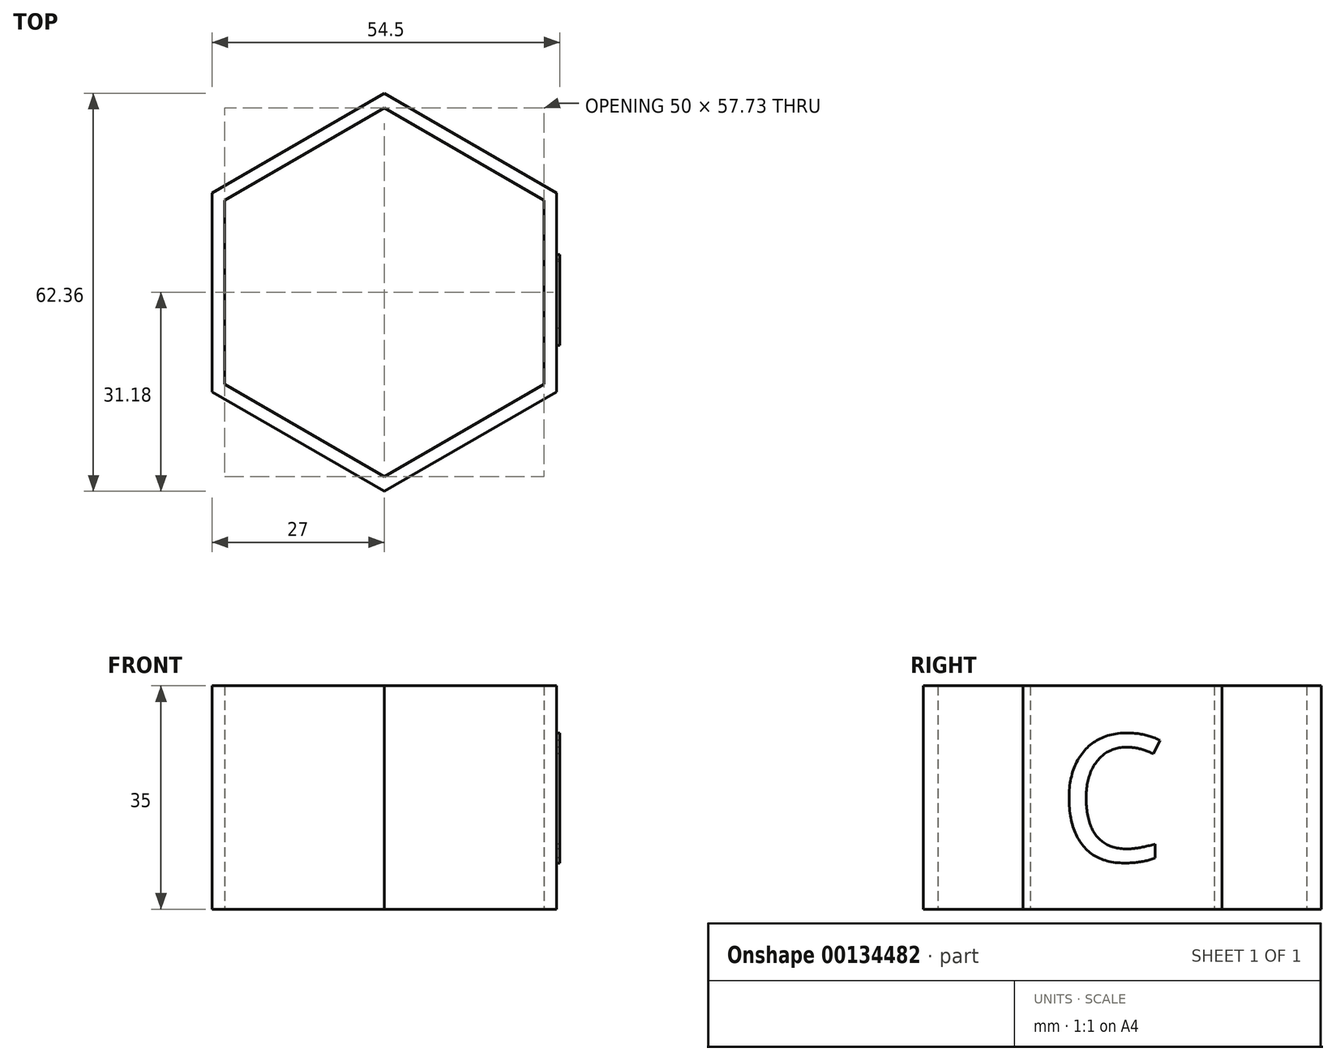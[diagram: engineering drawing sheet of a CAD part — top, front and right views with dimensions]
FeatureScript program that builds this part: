
annotation { "Feature Type Name" : "Feature", "Feature Type Description" : "" }
export const myFeature = defineFeature(function(context is Context, id is Id, definition is map)
    precondition{}
    {
        {
            var Q0;
            Q0=qCreatedBy(makeId("Top.planeOp"),FACE);
            var sketch = newSketch(context, id + "F0", { "sketchPlane" : qUnion([Q0])});
            skCircle(sketch, "E0.cCircle", {"center": v(0, 0) * mm, "radius": 25 * mm, "construction": true});
            skLineSegment(sketch, "E0.0", {"start": v(25, 14.43) * mm, "end": v(25, -14.43) * mm});
            skLineSegment(sketch, "E0.1", {"start": v(25, -14.43) * mm, "end": v(0, -28.87) * mm});
            skLineSegment(sketch, "E0.2", {"start": v(0, -28.87) * mm, "end": v(-25, -14.43) * mm});
            skLineSegment(sketch, "E0.3", {"start": v(-25, -14.43) * mm, "end": v(-25, 14.43) * mm});
            skLineSegment(sketch, "E0.4", {"start": v(-25, 14.43) * mm, "end": v(0, 28.87) * mm});
            skLineSegment(sketch, "E0.5", {"start": v(0, 28.87) * mm, "end": v(25, 14.43) * mm});
            skPoint(sketch, "E0.0.midPoint", {"position": v(25, 0) * mm});
            skCircle(sketch, "E1.cCircle", {"center": v(0, 0) * mm, "radius": 27 * mm, "construction": true});
            skLineSegment(sketch, "E1.0", {"start": v(27, 15.59) * mm, "end": v(27, -15.59) * mm});
            skLineSegment(sketch, "E1.1", {"start": v(27, -15.59) * mm, "end": v(0, -31.18) * mm});
            skLineSegment(sketch, "E1.2", {"start": v(0, -31.18) * mm, "end": v(-27, -15.59) * mm});
            skLineSegment(sketch, "E1.3", {"start": v(-27, -15.59) * mm, "end": v(-27, 15.59) * mm});
            skLineSegment(sketch, "E1.4", {"start": v(-27, 15.59) * mm, "end": v(0, 31.18) * mm});
            skLineSegment(sketch, "E1.5", {"start": v(0, 31.18) * mm, "end": v(27, 15.59) * mm});
            skPoint(sketch, "E1.0.midPoint", {"position": v(27, 0) * mm});
            skSolve(sketch);
        }
        {
            var Q0;
            Q0 = qSketchRegion(id + "F0", true);
            extrude(context, id + "F1", {"entities" : qUnion([Q0]), "depth" : 35 * mm});
        }
        {
            var Q0;
            Q0=makeQuery(id+"F1.opExtrude","SWEPT_FACE",FACE,{"disambiguationData":[OSD([sQuery(id+"F0.wireOp",EDGE,"E1.0")])]});
            var sketch = newSketch(context, id + "F2", { "sketchPlane" : qUnion([Q0])});
            skText(sketch, "E2", { "text": "C", "fontName": "DroidSansMono.ttf"});
            skLineSegment(sketch, "E3", {"start": v(10.09, 17.5) * mm, "end": v(15.59, 17.5) * mm, "construction": true});
            const initialGuessF2  = {"E2": [-0.01009, 0.0075, 1, 0, 0.02]};
            skSetInitialGuess(sketch, initialGuessF2);
            skSolve(sketch);
        }
        {
            var Q0;
            Q0 = qSketchRegion(id + "F2", true);
            extrude(context, id + "F3", {"entities" : qUnion([Q0]), "operationType" : NewBodyOperationType.ADD, "depth" : 0.5 * mm});
        }
    });
